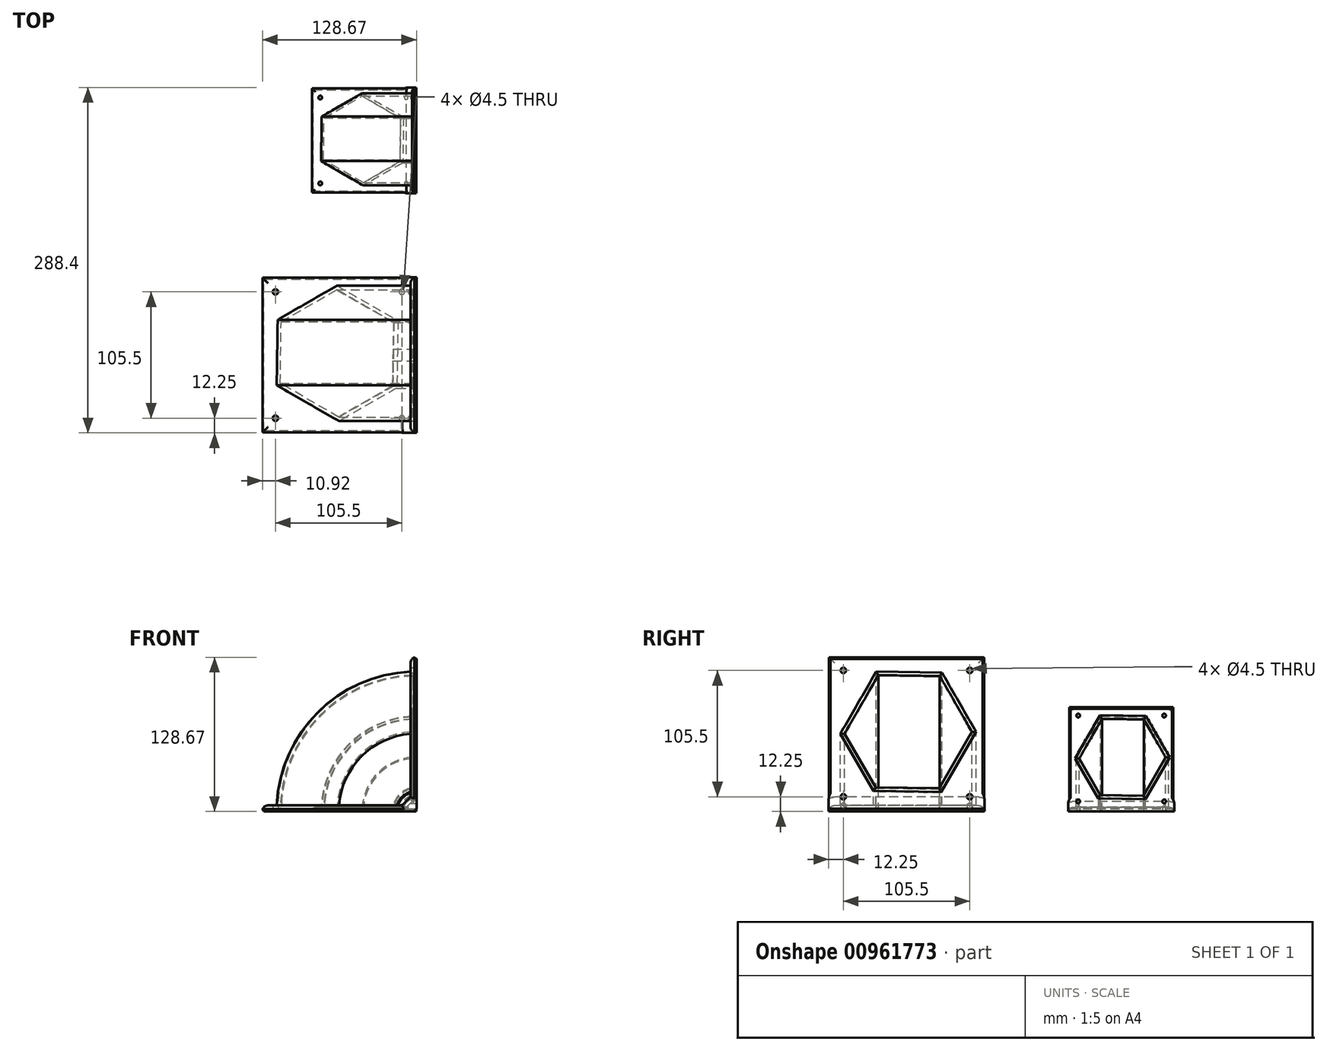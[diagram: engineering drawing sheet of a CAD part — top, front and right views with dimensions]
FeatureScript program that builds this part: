
annotation { "Feature Type Name" : "Feature", "Feature Type Description" : "" }
export const myFeature = defineFeature(function(context is Context, id is Id, definition is map)
    precondition{}
    {
        {
            var Q0;
            Q0=qCreatedBy(makeId("Top.planeOp"),FACE);
            var sketch = newSketch(context, id + "F0", { "sketchPlane" : qUnion([Q0])});
            skCircle(sketch, "E0", {"center": v(0, 0) * mm, "radius": 60 * mm, "construction": true});
            skLineSegment(sketch, "E1.bottom", {"start": v(64.01, -65) * mm, "end": v(-64.01, -65) * mm});
            skLineSegment(sketch, "E1.top", {"start": v(64.01, 65) * mm, "end": v(-64.01, 65) * mm});
            skLineSegment(sketch, "E1.left", {"start": v(64.01, -65) * mm, "end": v(64.01, 65) * mm});
            skLineSegment(sketch, "E1.right", {"start": v(-64.01, -65) * mm, "end": v(-64.01, 65) * mm});
            skCircle(sketch, "E2.0", {"center": v(0, 0) * mm, "radius": 55.2 * mm, "construction": true});
            skLineSegment(sketch, "E3.bottom", {"start": v(52.75, 52.75) * mm, "end": v(-52.75, 52.75) * mm, "construction": true});
            skLineSegment(sketch, "E3.top", {"start": v(52.75, -52.75) * mm, "end": v(-52.75, -52.75) * mm, "construction": true});
            skLineSegment(sketch, "E3.left", {"start": v(52.75, 52.75) * mm, "end": v(52.75, -52.75) * mm, "construction": true});
            skLineSegment(sketch, "E3.right", {"start": v(-52.75, 52.75) * mm, "end": v(-52.75, -52.75) * mm, "construction": true});
            skCircle(sketch, "E4", {"center": v(52.75, -52.75) * mm, "radius": 2.25 * mm});
            skCircle(sketch, "E5", {"center": v(-52.75, -52.75) * mm, "radius": 2.25 * mm});
            skCircle(sketch, "E6", {"center": v(-52.75, 52.75) * mm, "radius": 2.25 * mm});
            skCircle(sketch, "E7", {"center": v(52.75, 52.75) * mm, "radius": 2.25 * mm});
            skPoint(sketch, "E8.cCircle.perimeterSnap0", {"position": v(0, -52.75) * mm});
            skLineSegment(sketch, "E8.0", {"start": v(0, -55.2) * mm, "end": v(-51.87, -25.25) * mm});
            skPoint(sketch, "E8.0.startSnap0", {"position": v(0, -52.75) * mm});
            skLineSegment(sketch, "E8.1", {"start": v(-51.87, -25.25) * mm, "end": v(-51.03, 29.5) * mm});
            skLineSegment(sketch, "E8.2", {"start": v(-51.03, 29.5) * mm, "end": v(-1.63, 58.01) * mm});
            skLineSegment(sketch, "E8.3", {"start": v(-1.63, 58.01) * mm, "end": v(48.73, 28.94) * mm});
            skLineSegment(sketch, "E8.4", {"start": v(48.73, 28.94) * mm, "end": v(47.8, -27.6) * mm});
            skLineSegment(sketch, "E8.5", {"start": v(47.8, -27.6) * mm, "end": v(0, -55.2) * mm});
            skLineSegment(sketch, "E9.0", {"start": v(-48.84, -23.54) * mm, "end": v(-48.05, 27.74) * mm});
            skLineSegment(sketch, "E9.1", {"start": v(-1.63, 54.55) * mm, "end": v(45.7, 27.23) * mm});
            skLineSegment(sketch, "E9.2", {"start": v(45.7, 27.23) * mm, "end": v(44.83, -25.85) * mm});
            skLineSegment(sketch, "E9.3", {"start": v(-48.05, 27.74) * mm, "end": v(-1.63, 54.55) * mm});
            skLineSegment(sketch, "E9.4", {"start": v(44.83, -25.85) * mm, "end": v(0, -51.74) * mm});
            skLineSegment(sketch, "E9.5", {"start": v(0, -51.74) * mm, "end": v(-48.84, -23.54) * mm});
            skSolve(sketch);
        }
        {
            var Q0;
            Q0=qCreatedBy(makeId("Front.planeOp"),FACE);
            var sketch = newSketch(context, id + "F1", { "sketchPlane" : qUnion([Q0])});
            skLineSegment(sketch, "E10.bottom", {"start": v(0, 0) * mm, "end": v(65, 0) * mm, "construction": true});
            skLineSegment(sketch, "E10.top", {"start": v(0, 65) * mm, "end": v(65, 65) * mm, "construction": true});
            skLineSegment(sketch, "E10.left", {"start": v(0, 0) * mm, "end": v(0, 65) * mm, "construction": true});
            skLineSegment(sketch, "E10.right", {"start": v(65, 0) * mm, "end": v(65, 65) * mm, "construction": true});
            skArc(sketch, "E11", {"start": v(19.04, 45.96) * mm, "mid": v(4.95, 24.87) * mm, "end": v(0, 0) * mm});
            skLineSegment(sketch, "E12", {"start": v(0, 65) * mm, "end": v(65, 0) * mm, "construction": true});
            skSolve(sketch);
        }
        {
            var Q0;
            Q0=makeQuery(id+"F0.imprint","IMPRINT",FACE,{"disambiguationData":[TD([[makeQuery(id+"F0.imprint","IMPRINT",EDGE,{"derivedFrom":sQuery(id+"F0.wireOp",EDGE,"E8.0")}),-1.0]])]});
            var Q1;
            Q1=sQuery(id+"F1.wireOp",EDGE,"E11");
            sweep(context, id + "F2", {"profiles" : qUnion([Q0]), "path" : qUnion([Q1])});
        }
        {
            var Q0;
            Q0=makeQuery(id+"F0.imprint","IMPRINT",FACE,{"disambiguationData":[TD([[makeQuery(id+"F0.imprint","IMPRINT",EDGE,{"derivedFrom":sQuery(id+"F0.wireOp",EDGE,"E1.bottom")}),-1.0]])]});
            var Q1;
            Q1=makeQuery(id+"F0.imprint","IMPRINT",FACE,{"disambiguationData":[TD([[makeQuery(id+"F0.imprint","IMPRINT",EDGE,{"derivedFrom":sQuery(id+"F0.wireOp",EDGE,"E8.0")}),-1.0]])]});
            extrude(context, id + "F3", {"entities" : qUnion([Q0, Q1]), "operationType" : NewBodyOperationType.ADD, "depth" : 5 * mm, "offsetDistance" : 25 * mm});
        }
        {
            var Q0;
            Q0=makeQuery(id+"F2.opSweep","CAP_FACE",FACE,{"disambiguationData":[OSD([sQuery(id+"F0.wireOp",EDGE,"E0"),sQuery(id+"F0.wireOp",EDGE,"E2.0"),sQuery(id+"F1.wireOp",VERTEX,"E11.start")])],"isStart":false});
            cPlane(context, id + "F4", {"entities" : qUnion([Q0]), "cplaneType" : CPlaneType.OFFSET, "offset" : 0 * mm, "width" : 150 * mm, "height" : 150 * mm});
        }
        {
            var Q0;
            Q0=makeQuery(id+"F2.opSweep","SWEPT_BODY",BODY,{"disambiguationData":[OSD([sQuery(id+"F0.wireOp",EDGE,"E0"),sQuery(id+"F0.wireOp",EDGE,"E2.0"),sQuery(id+"F1.wireOp",EDGE,"E11")])]});
            var Q1;
            Q1=qCreatedBy(id+"F4.planeOp",FACE);
            mirror(context, id + "F5", {"operationType" : NewBodyOperationType.ADD, "entities" : qUnion([Q0]), "mirrorPlane" : qUnion([Q1])});
        }
        {
            var Q0;
            {var subQ0=sQuery(id+"F0.wireOp",EDGE,"E1.top");var subQ1=sQuery(id+"F0.wireOp",EDGE,"E1.bottom");var subQ3=sQuery(id+"F0.wireOp",EDGE,"E6");var subQ4=sQuery(id+"F0.wireOp",EDGE,"E2.0");var subQ5=sQuery(id+"F0.wireOp",EDGE,"E4");var subQ6=sQuery(id+"F0.wireOp",EDGE,"E1.left");var subQ7=sQuery(id+"F0.wireOp",EDGE,"E1.right");var subQ8=sQuery(id+"F0.wireOp",EDGE,"E5");var subQ9=sQuery(id+"F0.wireOp",EDGE,"E7");var subQ10=makeQuery(id+"F3.boolean.opBoolean","SPLIT",FACE,{"disambiguationData":[TD([makeQuery(id+"F3.opExtrude","SWEPT_FACE",FACE,{"disambiguationData":[OSD([subQ1])]})])],"derivedFrom":makeQuery(id+"F3.opExtrude","CAP_FACE",FACE,{"disambiguationData":[OSD([subQ1,subQ0,subQ6,subQ7,subQ4,subQ5,subQ8,subQ3,subQ9])],"isStart":false})});Q0=makeQuery(id+"F5.boolean.opBoolean","INTERSECT",EDGE,{"disambiguationData":[OD(0.0)],"derivedFrom":[subQ10,makeQuery(id+"F5.opPattern","COPY",FACE,{"derivedFrom":subQ10,"instanceName":"1"})]});}
            var Q1;
            {var subQ0=sQuery(id+"F0.wireOp",EDGE,"E1.top");var subQ1=sQuery(id+"F0.wireOp",EDGE,"E1.bottom");var subQ3=sQuery(id+"F0.wireOp",EDGE,"E6");var subQ4=sQuery(id+"F0.wireOp",EDGE,"E2.0");var subQ5=sQuery(id+"F0.wireOp",EDGE,"E4");var subQ6=sQuery(id+"F0.wireOp",EDGE,"E1.left");var subQ7=sQuery(id+"F0.wireOp",EDGE,"E1.right");var subQ8=sQuery(id+"F0.wireOp",EDGE,"E5");var subQ9=sQuery(id+"F0.wireOp",EDGE,"E7");var subQ10=makeQuery(id+"F3.boolean.opBoolean","SPLIT",FACE,{"disambiguationData":[TD([makeQuery(id+"F3.opExtrude","SWEPT_FACE",FACE,{"disambiguationData":[OSD([subQ1])]})])],"derivedFrom":makeQuery(id+"F3.opExtrude","CAP_FACE",FACE,{"disambiguationData":[OSD([subQ1,subQ0,subQ6,subQ7,subQ4,subQ5,subQ8,subQ3,subQ9])],"isStart":false})});Q1=makeQuery(id+"F5.boolean.opBoolean","INTERSECT",EDGE,{"disambiguationData":[OD(1.0)],"derivedFrom":[subQ10,makeQuery(id+"F5.opPattern","COPY",FACE,{"derivedFrom":subQ10,"instanceName":"1"})]});}
            chamfer(context, id + "F6", {"entities" : qUnion([Q0, Q1]), "width" : 7 * mm, "tangentPropagation" : true});
        }
        {
            var Q0;
            {var subQ0=sQuery(id+"F0.wireOp",EDGE,"E0");var subQ1=makeQuery(id+"F2.opSweep","SWEPT_FACE",FACE,{"disambiguationData":[OSD([subQ0,sQuery(id+"F1.wireOp",EDGE,"E11")])]});var subQ2=subQ1;var subQ3=sQuery(id+"F0.wireOp",EDGE,"E1.top");var subQ4=sQuery(id+"F0.wireOp",EDGE,"E1.bottom");var subQ5=sQuery(id+"F0.wireOp",EDGE,"E6");var subQ6=sQuery(id+"F0.wireOp",EDGE,"E2.0");var subQ7=sQuery(id+"F0.wireOp",EDGE,"E4");var subQ8=sQuery(id+"F0.wireOp",EDGE,"E1.left");var subQ9=sQuery(id+"F0.wireOp",EDGE,"E1.right");var subQ10=sQuery(id+"F0.wireOp",EDGE,"E5");var subQ11=sQuery(id+"F0.wireOp",EDGE,"E7");var subQ12=makeQuery(id+"F3.boolean.opBoolean","SPLIT",FACE,{"disambiguationData":[TD([makeQuery(id+"F3.opExtrude","SWEPT_FACE",FACE,{"disambiguationData":[OSD([subQ4])]})])],"derivedFrom":makeQuery(id+"F3.opExtrude","CAP_FACE",FACE,{"disambiguationData":[OSD([subQ4,subQ3,subQ8,subQ9,subQ6,subQ7,subQ10,subQ5,subQ11])],"isStart":false})});Q0=makeQuery(id+"F6.opChamfer","BLEND_EDGE",EDGE,{"blendedFrom":[makeQuery(id+"F5.boolean.opBoolean","INTERSECT",EDGE,{"disambiguationData":[OD(1.0)],"derivedFrom":[subQ12,makeQuery(id+"F5.opPattern","COPY",FACE,{"derivedFrom":subQ12,"instanceName":"1"})]}),makeQuery(id+"F5.boolean.opBoolean","MERGE",FACE,{"derivedFrom":[subQ2,makeQuery(id+"F5.opPattern","COPY",FACE,{"derivedFrom":subQ2,"instanceName":"1"})]})],"blendedInto":[makeQuery(id+"F5.boolean.opBoolean","MERGE",FACE,{"derivedFrom":[subQ2,makeQuery(id+"F5.opPattern","COPY",FACE,{"derivedFrom":subQ2,"instanceName":"1"})]})]});}
            var Q1;
            {var subQ0=sQuery(id+"F0.wireOp",EDGE,"E0");var subQ1=makeQuery(id+"F2.opSweep","SWEPT_FACE",FACE,{"disambiguationData":[OSD([subQ0,sQuery(id+"F1.wireOp",EDGE,"E11")])]});var subQ2=subQ1;var subQ3=sQuery(id+"F0.wireOp",EDGE,"E1.top");var subQ4=sQuery(id+"F0.wireOp",EDGE,"E1.bottom");var subQ5=sQuery(id+"F0.wireOp",EDGE,"E6");var subQ6=sQuery(id+"F0.wireOp",EDGE,"E2.0");var subQ7=sQuery(id+"F0.wireOp",EDGE,"E4");var subQ8=sQuery(id+"F0.wireOp",EDGE,"E1.left");var subQ9=sQuery(id+"F0.wireOp",EDGE,"E1.right");var subQ10=sQuery(id+"F0.wireOp",EDGE,"E5");var subQ11=sQuery(id+"F0.wireOp",EDGE,"E7");var subQ12=makeQuery(id+"F3.boolean.opBoolean","SPLIT",FACE,{"disambiguationData":[TD([makeQuery(id+"F3.opExtrude","SWEPT_FACE",FACE,{"disambiguationData":[OSD([subQ4])]})])],"derivedFrom":makeQuery(id+"F3.opExtrude","CAP_FACE",FACE,{"disambiguationData":[OSD([subQ4,subQ3,subQ8,subQ9,subQ6,subQ7,subQ10,subQ5,subQ11])],"isStart":false})});Q1=makeQuery(id+"F6.opChamfer","BLEND_EDGE",EDGE,{"blendedFrom":[makeQuery(id+"F5.boolean.opBoolean","INTERSECT",EDGE,{"disambiguationData":[OD(0.0)],"derivedFrom":[subQ12,makeQuery(id+"F5.opPattern","COPY",FACE,{"derivedFrom":subQ12,"instanceName":"1"})]}),makeQuery(id+"F5.boolean.opBoolean","MERGE",FACE,{"derivedFrom":[subQ2,makeQuery(id+"F5.opPattern","COPY",FACE,{"derivedFrom":subQ2,"instanceName":"1"})]})],"blendedInto":[makeQuery(id+"F5.boolean.opBoolean","MERGE",FACE,{"derivedFrom":[subQ2,makeQuery(id+"F5.opPattern","COPY",FACE,{"derivedFrom":subQ2,"instanceName":"1"})]})]});}
            var Q2;
            Q2=makeQuery(id+"F3.opExtrude","CAP_EDGE",EDGE,{"disambiguationData":[OSD([sQuery(id+"F0.wireOp",EDGE,"E1.bottom")])],"isStart":false});
            var Q3;
            Q3=makeQuery(id+"F5.opPattern","COPY",EDGE,{"derivedFrom":makeQuery(id+"F3.opExtrude","CAP_EDGE",EDGE,{"disambiguationData":[OSD([sQuery(id+"F0.wireOp",EDGE,"E1.bottom")])],"isStart":false}),"instanceName":"1"});
            var Q4;
            Q4=makeQuery(id+"F5.opPattern","COPY",EDGE,{"derivedFrom":makeQuery(id+"F3.opExtrude","CAP_EDGE",EDGE,{"disambiguationData":[OSD([sQuery(id+"F0.wireOp",EDGE,"E1.top")])],"isStart":false}),"instanceName":"1"});
            var Q5;
            Q5=makeQuery(id+"F5.opPattern","COPY",EDGE,{"derivedFrom":makeQuery(id+"F3.opExtrude","CAP_EDGE",EDGE,{"disambiguationData":[OSD([sQuery(id+"F0.wireOp",EDGE,"E1.right")])],"isStart":false}),"instanceName":"1"});
            var Q6;
            Q6=makeQuery(id+"F3.opExtrude","CAP_EDGE",EDGE,{"disambiguationData":[OSD([sQuery(id+"F0.wireOp",EDGE,"E1.top")])],"isStart":false});
            var Q7;
            {var subQ0=sQuery(id+"F0.wireOp",EDGE,"E1.top");var subQ1=makeQuery(id+"F3.opExtrude","SWEPT_FACE",FACE,{"disambiguationData":[OSD([subQ0])]});var subQ2=sQuery(id+"F0.wireOp",EDGE,"E1.bottom");var subQ4=sQuery(id+"F0.wireOp",EDGE,"E6");var subQ5=sQuery(id+"F0.wireOp",EDGE,"E2.0");var subQ6=sQuery(id+"F0.wireOp",EDGE,"E4");var subQ7=sQuery(id+"F0.wireOp",EDGE,"E1.left");var subQ8=sQuery(id+"F0.wireOp",EDGE,"E1.right");var subQ9=sQuery(id+"F0.wireOp",EDGE,"E5");var subQ10=sQuery(id+"F0.wireOp",EDGE,"E7");var subQ11=makeQuery(id+"F3.boolean.opBoolean","SPLIT",FACE,{"disambiguationData":[TD([makeQuery(id+"F3.opExtrude","SWEPT_FACE",FACE,{"disambiguationData":[OSD([subQ2])]})])],"derivedFrom":makeQuery(id+"F3.opExtrude","CAP_FACE",FACE,{"disambiguationData":[OSD([subQ2,subQ0,subQ7,subQ8,subQ5,subQ6,subQ9,subQ4,subQ10])],"isStart":false})});Q7=makeQuery(id+"F6.opChamfer","BLEND_EDGE",EDGE,{"blendedFrom":[makeQuery(id+"F5.boolean.opBoolean","INTERSECT",EDGE,{"disambiguationData":[OD(1.0)],"derivedFrom":[subQ11,makeQuery(id+"F5.opPattern","COPY",FACE,{"derivedFrom":subQ11,"instanceName":"1"})]}),makeQuery(id+"F5.boolean.opBoolean","MERGE",FACE,{"derivedFrom":[subQ1,makeQuery(id+"F5.opPattern","COPY",FACE,{"derivedFrom":subQ1,"instanceName":"1"})]})],"blendedInto":[makeQuery(id+"F5.boolean.opBoolean","MERGE",FACE,{"derivedFrom":[subQ1,makeQuery(id+"F5.opPattern","COPY",FACE,{"derivedFrom":subQ1,"instanceName":"1"})]})]});}
            var Q8;
            {var subQ0=sQuery(id+"F0.wireOp",EDGE,"E1.bottom");var subQ1=makeQuery(id+"F3.opExtrude","SWEPT_FACE",FACE,{"disambiguationData":[OSD([subQ0])]});var subQ2=sQuery(id+"F0.wireOp",EDGE,"E1.top");var subQ4=sQuery(id+"F0.wireOp",EDGE,"E6");var subQ5=sQuery(id+"F0.wireOp",EDGE,"E2.0");var subQ6=sQuery(id+"F0.wireOp",EDGE,"E4");var subQ7=sQuery(id+"F0.wireOp",EDGE,"E1.left");var subQ8=sQuery(id+"F0.wireOp",EDGE,"E1.right");var subQ9=sQuery(id+"F0.wireOp",EDGE,"E5");var subQ10=sQuery(id+"F0.wireOp",EDGE,"E7");var subQ11=makeQuery(id+"F3.boolean.opBoolean","SPLIT",FACE,{"disambiguationData":[TD([subQ1])],"derivedFrom":makeQuery(id+"F3.opExtrude","CAP_FACE",FACE,{"disambiguationData":[OSD([subQ0,subQ2,subQ7,subQ8,subQ5,subQ6,subQ9,subQ4,subQ10])],"isStart":false})});Q8=makeQuery(id+"F6.opChamfer","BLEND_EDGE",EDGE,{"blendedFrom":[makeQuery(id+"F5.boolean.opBoolean","INTERSECT",EDGE,{"disambiguationData":[OD(0.0)],"derivedFrom":[subQ11,makeQuery(id+"F5.opPattern","COPY",FACE,{"derivedFrom":subQ11,"instanceName":"1"})]}),makeQuery(id+"F5.boolean.opBoolean","MERGE",FACE,{"derivedFrom":[subQ1,makeQuery(id+"F5.opPattern","COPY",FACE,{"derivedFrom":subQ1,"instanceName":"1"})]})],"blendedInto":[makeQuery(id+"F5.boolean.opBoolean","MERGE",FACE,{"derivedFrom":[subQ1,makeQuery(id+"F5.opPattern","COPY",FACE,{"derivedFrom":subQ1,"instanceName":"1"})]})]});}
            var Q9;
            Q9=makeQuery(id+"F3.opExtrude","CAP_EDGE",EDGE,{"disambiguationData":[OSD([sQuery(id+"F0.wireOp",EDGE,"E1.right")])],"isStart":false});
            fillet(context, id + "F7", {"entities" : qUnion([Q0, Q1, Q2, Q3, Q4, Q5, Q6, Q7, Q8, Q9]), "radius" : 5 * mm, "tangentPropagation" : true, "allowEdgeOverflow" : false});
        }
        {
            var Q0;
            Q0=makeQuery(id+"F2.opSweep","SWEPT_BODY",BODY,{"disambiguationData":[OSD([sQuery(id+"F0.wireOp",EDGE,"E0"),sQuery(id+"F0.wireOp",EDGE,"E2.0"),sQuery(id+"F1.wireOp",EDGE,"E11")])]});
            transform(context, id + "F8", {"entities" : qUnion([Q0]), "transformType" : TransformType.TRANSLATION_3D, "dx" : 0 * mm, "dy" : 200 * mm, "dz" : 0 * mm, "makeCopy" : true});
        }
        {
            var Q0;
            Q0=makeQuery(id+"F8.opPattern","COPY",BODY,{"derivedFrom":makeQuery(id+"F2.opSweep","SWEPT_BODY",BODY,{"disambiguationData":[OSD([sQuery(id+"F0.wireOp",EDGE,"E0"),sQuery(id+"F0.wireOp",EDGE,"E2.0"),sQuery(id+"F1.wireOp",EDGE,"E11")])]}),"instanceName":"1"});
            var Q1;
            Q1=makeQuery(id+"F8.opPattern","COPY",VERTEX,{"derivedFrom":makeQuery(id+"F3.opExtrude","CAP_VERTEX",VERTEX,{"disambiguationData":[OSD([sQuery(id+"F0.wireOp",EDGE,"E1.bottom"),sQuery(id+"F0.wireOp",EDGE,"E1.left")])],"isStart":true}),"instanceName":"1"});
            transform(context, id + "F9", {"entities" : qUnion([Q0]), "transformType" : TransformType.SCALE_UNIFORMLY, "scale" : 0.68, "scalePoint" : qUnion([Q1]), "makeCopy" : false});
        }
        {
            var Q0;
            {var subQ0=sQuery(id+"F0.wireOp",EDGE,"E2.0");Q0=makeQuery(id+"F5.opPattern","COPY",FACE,{"derivedFrom":makeQuery(id+"F3.boolean.opBoolean","MERGE",FACE,{"derivedFrom":[makeQuery(id+"F2.opSweep","CAP_FACE",FACE,{"disambiguationData":[OSD([sQuery(id+"F0.wireOp",EDGE,"E0"),subQ0,sQuery(id+"F1.wireOp",VERTEX,"E11.end")])],"isStart":true}),makeQuery(id+"F3.opExtrude","CAP_FACE",FACE,{"disambiguationData":[OSD([sQuery(id+"F0.wireOp",EDGE,"E1.bottom"),sQuery(id+"F0.wireOp",EDGE,"E1.top"),sQuery(id+"F0.wireOp",EDGE,"E1.left"),sQuery(id+"F0.wireOp",EDGE,"E1.right"),subQ0,sQuery(id+"F0.wireOp",EDGE,"E4"),sQuery(id+"F0.wireOp",EDGE,"E5"),sQuery(id+"F0.wireOp",EDGE,"E6"),sQuery(id+"F0.wireOp",EDGE,"E7")])],"isStart":true})]}),"instanceName":"1"});}
            var sketch = newSketch(context, id + "F10", { "sketchPlane" : qUnion([Q0])});
            skArc(sketch, "E13", {"start": v(5, 0.99) * mm, "mid": v(0, 2.33) * mm, "end": v(-5, 0.99) * mm});
            skLineSegment(sketch, "E14", {"start": v(-5, 0.99) * mm, "end": v(-5, 0) * mm});
            skLineSegment(sketch, "E15", {"start": v(-5, 0) * mm, "end": v(5, 0) * mm});
            skLineSegment(sketch, "E16", {"start": v(5, 0) * mm, "end": v(5, 0.99) * mm});
            skSolve(sketch);
        }
        {
            var Q0;
            {var subQ0=sQuery(id+"F10.wireOp",EDGE,"E13");Q0=makeQuery(id+"F10.imprint","IMPRINT",FACE,{"disambiguationData":[TD([[makeQuery(id+"F10.imprint","IMPRINT",EDGE,{"derivedFrom":subQ0}),1.0]])]});}
            var Q1;
            {var subQ0=sQuery(id+"F10.wireOp",EDGE,"E14");Q1=makeQuery(id+"F10.imprint","IMPRINT",FACE,{"disambiguationData":[TD([[makeQuery(id+"F10.imprint","IMPRINT",EDGE,{"derivedFrom":subQ0}),1.0]])]});}
            extrude(context, id + "F11", {"entities" : qUnion([Q0, Q1]), "operationType" : NewBodyOperationType.REMOVE, "oppositeDirection" : true, "depth" : 25 * mm, "offsetDistance" : 25 * mm});
        }
        {
            var Q0;
            {var subQ1=sQuery(id+"F0.wireOp",EDGE,"E1.left");var subQ2=sQuery(id+"F0.wireOp",EDGE,"E1.top");var subQ3=makeQuery(id+"F3.opExtrude","SWEPT_FACE",FACE,{"disambiguationData":[OSD([subQ2])]});Q0=makeQuery(id+"F11.boolean.opBoolean","SPLIT",EDGE,{"disambiguationData":[TD([subQ3])],"derivedFrom":makeQuery(id+"F5.opPattern","COPY",EDGE,{"derivedFrom":makeQuery(id+"F3.opExtrude","CAP_EDGE",EDGE,{"disambiguationData":[OSD([subQ1])],"isStart":true}),"instanceName":"1"})});}
            var Q1;
            {var subQ1=sQuery(id+"F0.wireOp",EDGE,"E1.left");var subQ2=sQuery(id+"F0.wireOp",EDGE,"E1.bottom");var subQ3=makeQuery(id+"F3.opExtrude","SWEPT_FACE",FACE,{"disambiguationData":[OSD([subQ2])]});Q1=makeQuery(id+"F11.boolean.opBoolean","SPLIT",EDGE,{"disambiguationData":[TD([subQ3])],"derivedFrom":makeQuery(id+"F5.opPattern","COPY",EDGE,{"derivedFrom":makeQuery(id+"F3.opExtrude","CAP_EDGE",EDGE,{"disambiguationData":[OSD([subQ1])],"isStart":true}),"instanceName":"1"})});}
            var Q2;
            {var subQ0=sQuery(id+"F0.wireOp",EDGE,"E9.5");var subQ1=sQuery(id+"F0.wireOp",EDGE,"E9.4");var subQ2=sQuery(id+"F0.wireOp",EDGE,"E9.3");var subQ3=sQuery(id+"F0.wireOp",EDGE,"E9.2");var subQ4=sQuery(id+"F0.wireOp",EDGE,"E9.1");var subQ5=sQuery(id+"F0.wireOp",EDGE,"E9.0");var subQ6=sQuery(id+"F0.wireOp",EDGE,"E1.top");Q2=makeQuery(id+"F7.opFillet","BLEND_EDGE",EDGE,{"blendedFrom":[makeQuery(id+"F3.opExtrude","CAP_EDGE",EDGE,{"disambiguationData":[OSD([subQ6])],"isStart":false}),makeQuery(id+"F3.boolean.opBoolean","MERGE",FACE,{"derivedFrom":[makeQuery(id+"F2.opSweep","CAP_FACE",FACE,{"disambiguationData":[OSD([sQuery(id+"F0.wireOp",EDGE,"E8.0"),sQuery(id+"F0.wireOp",EDGE,"E8.1"),sQuery(id+"F0.wireOp",EDGE,"E8.2"),sQuery(id+"F0.wireOp",EDGE,"E8.3"),sQuery(id+"F0.wireOp",EDGE,"E8.4"),sQuery(id+"F0.wireOp",EDGE,"E8.5"),subQ5,subQ4,subQ3,subQ2,subQ1,subQ0,sQuery(id+"F1.wireOp",VERTEX,"E11.end")])],"isStart":true}),makeQuery(id+"F3.opExtrude","CAP_FACE",FACE,{"disambiguationData":[OSD([sQuery(id+"F0.wireOp",EDGE,"E1.bottom"),subQ6,sQuery(id+"F0.wireOp",EDGE,"E1.left"),sQuery(id+"F0.wireOp",EDGE,"E1.right"),sQuery(id+"F0.wireOp",EDGE,"E4"),sQuery(id+"F0.wireOp",EDGE,"E5"),sQuery(id+"F0.wireOp",EDGE,"E6"),sQuery(id+"F0.wireOp",EDGE,"E7"),subQ5,subQ4,subQ3,subQ2,subQ1,subQ0])],"isStart":true})]})],"blendedInto":[makeQuery(id+"F3.boolean.opBoolean","MERGE",FACE,{"derivedFrom":[makeQuery(id+"F2.opSweep","CAP_FACE",FACE,{"disambiguationData":[OSD([sQuery(id+"F0.wireOp",EDGE,"E8.0"),sQuery(id+"F0.wireOp",EDGE,"E8.1"),sQuery(id+"F0.wireOp",EDGE,"E8.2"),sQuery(id+"F0.wireOp",EDGE,"E8.3"),sQuery(id+"F0.wireOp",EDGE,"E8.4"),sQuery(id+"F0.wireOp",EDGE,"E8.5"),subQ5,subQ4,subQ3,subQ2,subQ1,subQ0,sQuery(id+"F1.wireOp",VERTEX,"E11.end")])],"isStart":true}),makeQuery(id+"F3.opExtrude","CAP_FACE",FACE,{"disambiguationData":[OSD([sQuery(id+"F0.wireOp",EDGE,"E1.bottom"),subQ6,sQuery(id+"F0.wireOp",EDGE,"E1.left"),sQuery(id+"F0.wireOp",EDGE,"E1.right"),sQuery(id+"F0.wireOp",EDGE,"E4"),sQuery(id+"F0.wireOp",EDGE,"E5"),sQuery(id+"F0.wireOp",EDGE,"E6"),sQuery(id+"F0.wireOp",EDGE,"E7"),subQ5,subQ4,subQ3,subQ2,subQ1,subQ0])],"isStart":true})]})]});}
            var Q3;
            {var subQ0=sQuery(id+"F0.wireOp",EDGE,"E9.5");var subQ1=sQuery(id+"F0.wireOp",EDGE,"E9.4");var subQ2=sQuery(id+"F0.wireOp",EDGE,"E9.3");var subQ3=sQuery(id+"F0.wireOp",EDGE,"E9.2");var subQ4=sQuery(id+"F0.wireOp",EDGE,"E9.1");var subQ5=sQuery(id+"F0.wireOp",EDGE,"E9.0");var subQ6=sQuery(id+"F0.wireOp",EDGE,"E1.right");Q3=makeQuery(id+"F7.opFillet","BLEND_EDGE",EDGE,{"blendedFrom":[makeQuery(id+"F3.opExtrude","CAP_EDGE",EDGE,{"disambiguationData":[OSD([subQ6])],"isStart":false}),makeQuery(id+"F3.boolean.opBoolean","MERGE",FACE,{"derivedFrom":[makeQuery(id+"F2.opSweep","CAP_FACE",FACE,{"disambiguationData":[OSD([sQuery(id+"F0.wireOp",EDGE,"E8.0"),sQuery(id+"F0.wireOp",EDGE,"E8.1"),sQuery(id+"F0.wireOp",EDGE,"E8.2"),sQuery(id+"F0.wireOp",EDGE,"E8.3"),sQuery(id+"F0.wireOp",EDGE,"E8.4"),sQuery(id+"F0.wireOp",EDGE,"E8.5"),subQ5,subQ4,subQ3,subQ2,subQ1,subQ0,sQuery(id+"F1.wireOp",VERTEX,"E11.end")])],"isStart":true}),makeQuery(id+"F3.opExtrude","CAP_FACE",FACE,{"disambiguationData":[OSD([sQuery(id+"F0.wireOp",EDGE,"E1.bottom"),sQuery(id+"F0.wireOp",EDGE,"E1.top"),sQuery(id+"F0.wireOp",EDGE,"E1.left"),subQ6,sQuery(id+"F0.wireOp",EDGE,"E4"),sQuery(id+"F0.wireOp",EDGE,"E5"),sQuery(id+"F0.wireOp",EDGE,"E6"),sQuery(id+"F0.wireOp",EDGE,"E7"),subQ5,subQ4,subQ3,subQ2,subQ1,subQ0])],"isStart":true})]})],"blendedInto":[makeQuery(id+"F3.boolean.opBoolean","MERGE",FACE,{"derivedFrom":[makeQuery(id+"F2.opSweep","CAP_FACE",FACE,{"disambiguationData":[OSD([sQuery(id+"F0.wireOp",EDGE,"E8.0"),sQuery(id+"F0.wireOp",EDGE,"E8.1"),sQuery(id+"F0.wireOp",EDGE,"E8.2"),sQuery(id+"F0.wireOp",EDGE,"E8.3"),sQuery(id+"F0.wireOp",EDGE,"E8.4"),sQuery(id+"F0.wireOp",EDGE,"E8.5"),subQ5,subQ4,subQ3,subQ2,subQ1,subQ0,sQuery(id+"F1.wireOp",VERTEX,"E11.end")])],"isStart":true}),makeQuery(id+"F3.opExtrude","CAP_FACE",FACE,{"disambiguationData":[OSD([sQuery(id+"F0.wireOp",EDGE,"E1.bottom"),sQuery(id+"F0.wireOp",EDGE,"E1.top"),sQuery(id+"F0.wireOp",EDGE,"E1.left"),subQ6,sQuery(id+"F0.wireOp",EDGE,"E4"),sQuery(id+"F0.wireOp",EDGE,"E5"),sQuery(id+"F0.wireOp",EDGE,"E6"),sQuery(id+"F0.wireOp",EDGE,"E7"),subQ5,subQ4,subQ3,subQ2,subQ1,subQ0])],"isStart":true})]})]});}
            var Q4;
            {var subQ0=sQuery(id+"F0.wireOp",EDGE,"E9.5");var subQ1=sQuery(id+"F0.wireOp",EDGE,"E9.4");var subQ2=sQuery(id+"F0.wireOp",EDGE,"E9.3");var subQ3=sQuery(id+"F0.wireOp",EDGE,"E9.2");var subQ4=sQuery(id+"F0.wireOp",EDGE,"E9.1");var subQ5=sQuery(id+"F0.wireOp",EDGE,"E9.0");var subQ6=sQuery(id+"F0.wireOp",EDGE,"E1.bottom");Q4=makeQuery(id+"F7.opFillet","BLEND_EDGE",EDGE,{"blendedFrom":[makeQuery(id+"F3.opExtrude","CAP_EDGE",EDGE,{"disambiguationData":[OSD([subQ6])],"isStart":false}),makeQuery(id+"F3.boolean.opBoolean","MERGE",FACE,{"derivedFrom":[makeQuery(id+"F2.opSweep","CAP_FACE",FACE,{"disambiguationData":[OSD([sQuery(id+"F0.wireOp",EDGE,"E8.0"),sQuery(id+"F0.wireOp",EDGE,"E8.1"),sQuery(id+"F0.wireOp",EDGE,"E8.2"),sQuery(id+"F0.wireOp",EDGE,"E8.3"),sQuery(id+"F0.wireOp",EDGE,"E8.4"),sQuery(id+"F0.wireOp",EDGE,"E8.5"),subQ5,subQ4,subQ3,subQ2,subQ1,subQ0,sQuery(id+"F1.wireOp",VERTEX,"E11.end")])],"isStart":true}),makeQuery(id+"F3.opExtrude","CAP_FACE",FACE,{"disambiguationData":[OSD([subQ6,sQuery(id+"F0.wireOp",EDGE,"E1.top"),sQuery(id+"F0.wireOp",EDGE,"E1.left"),sQuery(id+"F0.wireOp",EDGE,"E1.right"),sQuery(id+"F0.wireOp",EDGE,"E4"),sQuery(id+"F0.wireOp",EDGE,"E5"),sQuery(id+"F0.wireOp",EDGE,"E6"),sQuery(id+"F0.wireOp",EDGE,"E7"),subQ5,subQ4,subQ3,subQ2,subQ1,subQ0])],"isStart":true})]})],"blendedInto":[makeQuery(id+"F3.boolean.opBoolean","MERGE",FACE,{"derivedFrom":[makeQuery(id+"F2.opSweep","CAP_FACE",FACE,{"disambiguationData":[OSD([sQuery(id+"F0.wireOp",EDGE,"E8.0"),sQuery(id+"F0.wireOp",EDGE,"E8.1"),sQuery(id+"F0.wireOp",EDGE,"E8.2"),sQuery(id+"F0.wireOp",EDGE,"E8.3"),sQuery(id+"F0.wireOp",EDGE,"E8.4"),sQuery(id+"F0.wireOp",EDGE,"E8.5"),subQ5,subQ4,subQ3,subQ2,subQ1,subQ0,sQuery(id+"F1.wireOp",VERTEX,"E11.end")])],"isStart":true}),makeQuery(id+"F3.opExtrude","CAP_FACE",FACE,{"disambiguationData":[OSD([subQ6,sQuery(id+"F0.wireOp",EDGE,"E1.top"),sQuery(id+"F0.wireOp",EDGE,"E1.left"),sQuery(id+"F0.wireOp",EDGE,"E1.right"),sQuery(id+"F0.wireOp",EDGE,"E4"),sQuery(id+"F0.wireOp",EDGE,"E5"),sQuery(id+"F0.wireOp",EDGE,"E6"),sQuery(id+"F0.wireOp",EDGE,"E7"),subQ5,subQ4,subQ3,subQ2,subQ1,subQ0])],"isStart":true})]})]});}
            var Q5;
            {var subQ0=sQuery(id+"F0.wireOp",EDGE,"E9.5");var subQ1=sQuery(id+"F0.wireOp",EDGE,"E9.4");var subQ2=sQuery(id+"F0.wireOp",EDGE,"E9.3");var subQ3=sQuery(id+"F0.wireOp",EDGE,"E9.2");var subQ4=sQuery(id+"F0.wireOp",EDGE,"E9.1");var subQ5=sQuery(id+"F0.wireOp",EDGE,"E9.0");var subQ6=sQuery(id+"F0.wireOp",EDGE,"E1.bottom");Q5=makeQuery(id+"F8.opPattern","COPY",EDGE,{"derivedFrom":makeQuery(id+"F7.opFillet","BLEND_EDGE",EDGE,{"blendedFrom":[makeQuery(id+"F3.opExtrude","CAP_EDGE",EDGE,{"disambiguationData":[OSD([subQ6])],"isStart":false}),makeQuery(id+"F3.boolean.opBoolean","MERGE",FACE,{"derivedFrom":[makeQuery(id+"F2.opSweep","CAP_FACE",FACE,{"disambiguationData":[OSD([sQuery(id+"F0.wireOp",EDGE,"E8.0"),sQuery(id+"F0.wireOp",EDGE,"E8.1"),sQuery(id+"F0.wireOp",EDGE,"E8.2"),sQuery(id+"F0.wireOp",EDGE,"E8.3"),sQuery(id+"F0.wireOp",EDGE,"E8.4"),sQuery(id+"F0.wireOp",EDGE,"E8.5"),subQ5,subQ4,subQ3,subQ2,subQ1,subQ0,sQuery(id+"F1.wireOp",VERTEX,"E11.end")])],"isStart":true}),makeQuery(id+"F3.opExtrude","CAP_FACE",FACE,{"disambiguationData":[OSD([subQ6,sQuery(id+"F0.wireOp",EDGE,"E1.top"),sQuery(id+"F0.wireOp",EDGE,"E1.left"),sQuery(id+"F0.wireOp",EDGE,"E1.right"),sQuery(id+"F0.wireOp",EDGE,"E4"),sQuery(id+"F0.wireOp",EDGE,"E5"),sQuery(id+"F0.wireOp",EDGE,"E6"),sQuery(id+"F0.wireOp",EDGE,"E7"),subQ5,subQ4,subQ3,subQ2,subQ1,subQ0])],"isStart":true})]})],"blendedInto":[makeQuery(id+"F3.boolean.opBoolean","MERGE",FACE,{"derivedFrom":[makeQuery(id+"F2.opSweep","CAP_FACE",FACE,{"disambiguationData":[OSD([sQuery(id+"F0.wireOp",EDGE,"E8.0"),sQuery(id+"F0.wireOp",EDGE,"E8.1"),sQuery(id+"F0.wireOp",EDGE,"E8.2"),sQuery(id+"F0.wireOp",EDGE,"E8.3"),sQuery(id+"F0.wireOp",EDGE,"E8.4"),sQuery(id+"F0.wireOp",EDGE,"E8.5"),subQ5,subQ4,subQ3,subQ2,subQ1,subQ0,sQuery(id+"F1.wireOp",VERTEX,"E11.end")])],"isStart":true}),makeQuery(id+"F3.opExtrude","CAP_FACE",FACE,{"disambiguationData":[OSD([subQ6,sQuery(id+"F0.wireOp",EDGE,"E1.top"),sQuery(id+"F0.wireOp",EDGE,"E1.left"),sQuery(id+"F0.wireOp",EDGE,"E1.right"),sQuery(id+"F0.wireOp",EDGE,"E4"),sQuery(id+"F0.wireOp",EDGE,"E5"),sQuery(id+"F0.wireOp",EDGE,"E6"),sQuery(id+"F0.wireOp",EDGE,"E7"),subQ5,subQ4,subQ3,subQ2,subQ1,subQ0])],"isStart":true})]})]}),"instanceName":"1"});}
            var Q6;
            {var subQ0=sQuery(id+"F0.wireOp",EDGE,"E9.5");var subQ1=sQuery(id+"F0.wireOp",EDGE,"E9.4");var subQ2=sQuery(id+"F0.wireOp",EDGE,"E9.3");var subQ3=sQuery(id+"F0.wireOp",EDGE,"E9.2");var subQ4=sQuery(id+"F0.wireOp",EDGE,"E9.1");var subQ5=sQuery(id+"F0.wireOp",EDGE,"E9.0");var subQ6=sQuery(id+"F0.wireOp",EDGE,"E1.right");Q6=makeQuery(id+"F8.opPattern","COPY",EDGE,{"derivedFrom":makeQuery(id+"F7.opFillet","BLEND_EDGE",EDGE,{"blendedFrom":[makeQuery(id+"F3.opExtrude","CAP_EDGE",EDGE,{"disambiguationData":[OSD([subQ6])],"isStart":false}),makeQuery(id+"F3.boolean.opBoolean","MERGE",FACE,{"derivedFrom":[makeQuery(id+"F2.opSweep","CAP_FACE",FACE,{"disambiguationData":[OSD([sQuery(id+"F0.wireOp",EDGE,"E8.0"),sQuery(id+"F0.wireOp",EDGE,"E8.1"),sQuery(id+"F0.wireOp",EDGE,"E8.2"),sQuery(id+"F0.wireOp",EDGE,"E8.3"),sQuery(id+"F0.wireOp",EDGE,"E8.4"),sQuery(id+"F0.wireOp",EDGE,"E8.5"),subQ5,subQ4,subQ3,subQ2,subQ1,subQ0,sQuery(id+"F1.wireOp",VERTEX,"E11.end")])],"isStart":true}),makeQuery(id+"F3.opExtrude","CAP_FACE",FACE,{"disambiguationData":[OSD([sQuery(id+"F0.wireOp",EDGE,"E1.bottom"),sQuery(id+"F0.wireOp",EDGE,"E1.top"),sQuery(id+"F0.wireOp",EDGE,"E1.left"),subQ6,sQuery(id+"F0.wireOp",EDGE,"E4"),sQuery(id+"F0.wireOp",EDGE,"E5"),sQuery(id+"F0.wireOp",EDGE,"E6"),sQuery(id+"F0.wireOp",EDGE,"E7"),subQ5,subQ4,subQ3,subQ2,subQ1,subQ0])],"isStart":true})]})],"blendedInto":[makeQuery(id+"F3.boolean.opBoolean","MERGE",FACE,{"derivedFrom":[makeQuery(id+"F2.opSweep","CAP_FACE",FACE,{"disambiguationData":[OSD([sQuery(id+"F0.wireOp",EDGE,"E8.0"),sQuery(id+"F0.wireOp",EDGE,"E8.1"),sQuery(id+"F0.wireOp",EDGE,"E8.2"),sQuery(id+"F0.wireOp",EDGE,"E8.3"),sQuery(id+"F0.wireOp",EDGE,"E8.4"),sQuery(id+"F0.wireOp",EDGE,"E8.5"),subQ5,subQ4,subQ3,subQ2,subQ1,subQ0,sQuery(id+"F1.wireOp",VERTEX,"E11.end")])],"isStart":true}),makeQuery(id+"F3.opExtrude","CAP_FACE",FACE,{"disambiguationData":[OSD([sQuery(id+"F0.wireOp",EDGE,"E1.bottom"),sQuery(id+"F0.wireOp",EDGE,"E1.top"),sQuery(id+"F0.wireOp",EDGE,"E1.left"),subQ6,sQuery(id+"F0.wireOp",EDGE,"E4"),sQuery(id+"F0.wireOp",EDGE,"E5"),sQuery(id+"F0.wireOp",EDGE,"E6"),sQuery(id+"F0.wireOp",EDGE,"E7"),subQ5,subQ4,subQ3,subQ2,subQ1,subQ0])],"isStart":true})]})]}),"instanceName":"1"});}
            var Q7;
            {var subQ0=sQuery(id+"F0.wireOp",EDGE,"E9.5");var subQ1=sQuery(id+"F0.wireOp",EDGE,"E9.4");var subQ2=sQuery(id+"F0.wireOp",EDGE,"E9.3");var subQ3=sQuery(id+"F0.wireOp",EDGE,"E9.2");var subQ4=sQuery(id+"F0.wireOp",EDGE,"E9.1");var subQ5=sQuery(id+"F0.wireOp",EDGE,"E9.0");var subQ6=sQuery(id+"F0.wireOp",EDGE,"E1.top");Q7=makeQuery(id+"F8.opPattern","COPY",EDGE,{"derivedFrom":makeQuery(id+"F7.opFillet","BLEND_EDGE",EDGE,{"blendedFrom":[makeQuery(id+"F3.opExtrude","CAP_EDGE",EDGE,{"disambiguationData":[OSD([subQ6])],"isStart":false}),makeQuery(id+"F3.boolean.opBoolean","MERGE",FACE,{"derivedFrom":[makeQuery(id+"F2.opSweep","CAP_FACE",FACE,{"disambiguationData":[OSD([sQuery(id+"F0.wireOp",EDGE,"E8.0"),sQuery(id+"F0.wireOp",EDGE,"E8.1"),sQuery(id+"F0.wireOp",EDGE,"E8.2"),sQuery(id+"F0.wireOp",EDGE,"E8.3"),sQuery(id+"F0.wireOp",EDGE,"E8.4"),sQuery(id+"F0.wireOp",EDGE,"E8.5"),subQ5,subQ4,subQ3,subQ2,subQ1,subQ0,sQuery(id+"F1.wireOp",VERTEX,"E11.end")])],"isStart":true}),makeQuery(id+"F3.opExtrude","CAP_FACE",FACE,{"disambiguationData":[OSD([sQuery(id+"F0.wireOp",EDGE,"E1.bottom"),subQ6,sQuery(id+"F0.wireOp",EDGE,"E1.left"),sQuery(id+"F0.wireOp",EDGE,"E1.right"),sQuery(id+"F0.wireOp",EDGE,"E4"),sQuery(id+"F0.wireOp",EDGE,"E5"),sQuery(id+"F0.wireOp",EDGE,"E6"),sQuery(id+"F0.wireOp",EDGE,"E7"),subQ5,subQ4,subQ3,subQ2,subQ1,subQ0])],"isStart":true})]})],"blendedInto":[makeQuery(id+"F3.boolean.opBoolean","MERGE",FACE,{"derivedFrom":[makeQuery(id+"F2.opSweep","CAP_FACE",FACE,{"disambiguationData":[OSD([sQuery(id+"F0.wireOp",EDGE,"E8.0"),sQuery(id+"F0.wireOp",EDGE,"E8.1"),sQuery(id+"F0.wireOp",EDGE,"E8.2"),sQuery(id+"F0.wireOp",EDGE,"E8.3"),sQuery(id+"F0.wireOp",EDGE,"E8.4"),sQuery(id+"F0.wireOp",EDGE,"E8.5"),subQ5,subQ4,subQ3,subQ2,subQ1,subQ0,sQuery(id+"F1.wireOp",VERTEX,"E11.end")])],"isStart":true}),makeQuery(id+"F3.opExtrude","CAP_FACE",FACE,{"disambiguationData":[OSD([sQuery(id+"F0.wireOp",EDGE,"E1.bottom"),subQ6,sQuery(id+"F0.wireOp",EDGE,"E1.left"),sQuery(id+"F0.wireOp",EDGE,"E1.right"),sQuery(id+"F0.wireOp",EDGE,"E4"),sQuery(id+"F0.wireOp",EDGE,"E5"),sQuery(id+"F0.wireOp",EDGE,"E6"),sQuery(id+"F0.wireOp",EDGE,"E7"),subQ5,subQ4,subQ3,subQ2,subQ1,subQ0])],"isStart":true})]})]}),"instanceName":"1"});}
            var Q8;
            {var subQ0=makeQuery(id+"F3.opExtrude","SWEPT_FACE",FACE,{"disambiguationData":[OSD([sQuery(id+"F0.wireOp",EDGE,"E1.left")])]});Q8=makeQuery(id+"F8.opPattern","COPY",EDGE,{"derivedFrom":makeQuery(id+"F5.boolean.opBoolean","INTERSECT",EDGE,{"derivedFrom":[subQ0,makeQuery(id+"F5.opPattern","COPY",FACE,{"derivedFrom":subQ0,"instanceName":"1"})]}),"instanceName":"1"});}
            var Q9;
            {var subQ0=sQuery(id+"F0.wireOp",EDGE,"E9.5");var subQ1=sQuery(id+"F0.wireOp",EDGE,"E9.4");var subQ2=sQuery(id+"F0.wireOp",EDGE,"E9.3");var subQ3=sQuery(id+"F0.wireOp",EDGE,"E9.2");var subQ4=sQuery(id+"F0.wireOp",EDGE,"E9.1");var subQ5=sQuery(id+"F0.wireOp",EDGE,"E9.0");var subQ6=sQuery(id+"F0.wireOp",EDGE,"E1.top");Q9=makeQuery(id+"F8.opPattern","COPY",EDGE,{"derivedFrom":makeQuery(id+"F7.opFillet","BLEND_EDGE",EDGE,{"blendedFrom":[makeQuery(id+"F5.opPattern","COPY",EDGE,{"derivedFrom":makeQuery(id+"F3.opExtrude","CAP_EDGE",EDGE,{"disambiguationData":[OSD([subQ6])],"isStart":false}),"instanceName":"1"}),makeQuery(id+"F5.opPattern","COPY",FACE,{"derivedFrom":makeQuery(id+"F3.boolean.opBoolean","MERGE",FACE,{"derivedFrom":[makeQuery(id+"F2.opSweep","CAP_FACE",FACE,{"disambiguationData":[OSD([sQuery(id+"F0.wireOp",EDGE,"E8.0"),sQuery(id+"F0.wireOp",EDGE,"E8.1"),sQuery(id+"F0.wireOp",EDGE,"E8.2"),sQuery(id+"F0.wireOp",EDGE,"E8.3"),sQuery(id+"F0.wireOp",EDGE,"E8.4"),sQuery(id+"F0.wireOp",EDGE,"E8.5"),subQ5,subQ4,subQ3,subQ2,subQ1,subQ0,sQuery(id+"F1.wireOp",VERTEX,"E11.end")])],"isStart":true}),makeQuery(id+"F3.opExtrude","CAP_FACE",FACE,{"disambiguationData":[OSD([sQuery(id+"F0.wireOp",EDGE,"E1.bottom"),subQ6,sQuery(id+"F0.wireOp",EDGE,"E1.left"),sQuery(id+"F0.wireOp",EDGE,"E1.right"),sQuery(id+"F0.wireOp",EDGE,"E4"),sQuery(id+"F0.wireOp",EDGE,"E5"),sQuery(id+"F0.wireOp",EDGE,"E6"),sQuery(id+"F0.wireOp",EDGE,"E7"),subQ5,subQ4,subQ3,subQ2,subQ1,subQ0])],"isStart":true})]}),"instanceName":"1"})],"blendedInto":[makeQuery(id+"F5.opPattern","COPY",FACE,{"derivedFrom":makeQuery(id+"F3.boolean.opBoolean","MERGE",FACE,{"derivedFrom":[makeQuery(id+"F2.opSweep","CAP_FACE",FACE,{"disambiguationData":[OSD([sQuery(id+"F0.wireOp",EDGE,"E8.0"),sQuery(id+"F0.wireOp",EDGE,"E8.1"),sQuery(id+"F0.wireOp",EDGE,"E8.2"),sQuery(id+"F0.wireOp",EDGE,"E8.3"),sQuery(id+"F0.wireOp",EDGE,"E8.4"),sQuery(id+"F0.wireOp",EDGE,"E8.5"),subQ5,subQ4,subQ3,subQ2,subQ1,subQ0,sQuery(id+"F1.wireOp",VERTEX,"E11.end")])],"isStart":true}),makeQuery(id+"F3.opExtrude","CAP_FACE",FACE,{"disambiguationData":[OSD([sQuery(id+"F0.wireOp",EDGE,"E1.bottom"),subQ6,sQuery(id+"F0.wireOp",EDGE,"E1.left"),sQuery(id+"F0.wireOp",EDGE,"E1.right"),sQuery(id+"F0.wireOp",EDGE,"E4"),sQuery(id+"F0.wireOp",EDGE,"E5"),sQuery(id+"F0.wireOp",EDGE,"E6"),sQuery(id+"F0.wireOp",EDGE,"E7"),subQ5,subQ4,subQ3,subQ2,subQ1,subQ0])],"isStart":true})]}),"instanceName":"1"})]}),"instanceName":"1"});}
            var Q10;
            {var subQ0=sQuery(id+"F0.wireOp",EDGE,"E9.5");var subQ1=sQuery(id+"F0.wireOp",EDGE,"E9.4");var subQ2=sQuery(id+"F0.wireOp",EDGE,"E9.3");var subQ3=sQuery(id+"F0.wireOp",EDGE,"E9.2");var subQ4=sQuery(id+"F0.wireOp",EDGE,"E9.1");var subQ5=sQuery(id+"F0.wireOp",EDGE,"E9.0");var subQ6=sQuery(id+"F0.wireOp",EDGE,"E1.bottom");Q10=makeQuery(id+"F8.opPattern","COPY",EDGE,{"derivedFrom":makeQuery(id+"F7.opFillet","BLEND_EDGE",EDGE,{"blendedFrom":[makeQuery(id+"F5.opPattern","COPY",EDGE,{"derivedFrom":makeQuery(id+"F3.opExtrude","CAP_EDGE",EDGE,{"disambiguationData":[OSD([subQ6])],"isStart":false}),"instanceName":"1"}),makeQuery(id+"F5.opPattern","COPY",FACE,{"derivedFrom":makeQuery(id+"F3.boolean.opBoolean","MERGE",FACE,{"derivedFrom":[makeQuery(id+"F2.opSweep","CAP_FACE",FACE,{"disambiguationData":[OSD([sQuery(id+"F0.wireOp",EDGE,"E8.0"),sQuery(id+"F0.wireOp",EDGE,"E8.1"),sQuery(id+"F0.wireOp",EDGE,"E8.2"),sQuery(id+"F0.wireOp",EDGE,"E8.3"),sQuery(id+"F0.wireOp",EDGE,"E8.4"),sQuery(id+"F0.wireOp",EDGE,"E8.5"),subQ5,subQ4,subQ3,subQ2,subQ1,subQ0,sQuery(id+"F1.wireOp",VERTEX,"E11.end")])],"isStart":true}),makeQuery(id+"F3.opExtrude","CAP_FACE",FACE,{"disambiguationData":[OSD([subQ6,sQuery(id+"F0.wireOp",EDGE,"E1.top"),sQuery(id+"F0.wireOp",EDGE,"E1.left"),sQuery(id+"F0.wireOp",EDGE,"E1.right"),sQuery(id+"F0.wireOp",EDGE,"E4"),sQuery(id+"F0.wireOp",EDGE,"E5"),sQuery(id+"F0.wireOp",EDGE,"E6"),sQuery(id+"F0.wireOp",EDGE,"E7"),subQ5,subQ4,subQ3,subQ2,subQ1,subQ0])],"isStart":true})]}),"instanceName":"1"})],"blendedInto":[makeQuery(id+"F5.opPattern","COPY",FACE,{"derivedFrom":makeQuery(id+"F3.boolean.opBoolean","MERGE",FACE,{"derivedFrom":[makeQuery(id+"F2.opSweep","CAP_FACE",FACE,{"disambiguationData":[OSD([sQuery(id+"F0.wireOp",EDGE,"E8.0"),sQuery(id+"F0.wireOp",EDGE,"E8.1"),sQuery(id+"F0.wireOp",EDGE,"E8.2"),sQuery(id+"F0.wireOp",EDGE,"E8.3"),sQuery(id+"F0.wireOp",EDGE,"E8.4"),sQuery(id+"F0.wireOp",EDGE,"E8.5"),subQ5,subQ4,subQ3,subQ2,subQ1,subQ0,sQuery(id+"F1.wireOp",VERTEX,"E11.end")])],"isStart":true}),makeQuery(id+"F3.opExtrude","CAP_FACE",FACE,{"disambiguationData":[OSD([subQ6,sQuery(id+"F0.wireOp",EDGE,"E1.top"),sQuery(id+"F0.wireOp",EDGE,"E1.left"),sQuery(id+"F0.wireOp",EDGE,"E1.right"),sQuery(id+"F0.wireOp",EDGE,"E4"),sQuery(id+"F0.wireOp",EDGE,"E5"),sQuery(id+"F0.wireOp",EDGE,"E6"),sQuery(id+"F0.wireOp",EDGE,"E7"),subQ5,subQ4,subQ3,subQ2,subQ1,subQ0])],"isStart":true})]}),"instanceName":"1"})]}),"instanceName":"1"});}
            var Q11;
            {var subQ0=sQuery(id+"F0.wireOp",EDGE,"E9.5");var subQ1=sQuery(id+"F0.wireOp",EDGE,"E9.4");var subQ2=sQuery(id+"F0.wireOp",EDGE,"E9.3");var subQ3=sQuery(id+"F0.wireOp",EDGE,"E9.2");var subQ4=sQuery(id+"F0.wireOp",EDGE,"E9.1");var subQ5=sQuery(id+"F0.wireOp",EDGE,"E9.0");var subQ6=sQuery(id+"F0.wireOp",EDGE,"E1.right");Q11=makeQuery(id+"F8.opPattern","COPY",EDGE,{"derivedFrom":makeQuery(id+"F7.opFillet","BLEND_EDGE",EDGE,{"blendedFrom":[makeQuery(id+"F5.opPattern","COPY",EDGE,{"derivedFrom":makeQuery(id+"F3.opExtrude","CAP_EDGE",EDGE,{"disambiguationData":[OSD([subQ6])],"isStart":false}),"instanceName":"1"}),makeQuery(id+"F5.opPattern","COPY",FACE,{"derivedFrom":makeQuery(id+"F3.boolean.opBoolean","MERGE",FACE,{"derivedFrom":[makeQuery(id+"F2.opSweep","CAP_FACE",FACE,{"disambiguationData":[OSD([sQuery(id+"F0.wireOp",EDGE,"E8.0"),sQuery(id+"F0.wireOp",EDGE,"E8.1"),sQuery(id+"F0.wireOp",EDGE,"E8.2"),sQuery(id+"F0.wireOp",EDGE,"E8.3"),sQuery(id+"F0.wireOp",EDGE,"E8.4"),sQuery(id+"F0.wireOp",EDGE,"E8.5"),subQ5,subQ4,subQ3,subQ2,subQ1,subQ0,sQuery(id+"F1.wireOp",VERTEX,"E11.end")])],"isStart":true}),makeQuery(id+"F3.opExtrude","CAP_FACE",FACE,{"disambiguationData":[OSD([sQuery(id+"F0.wireOp",EDGE,"E1.bottom"),sQuery(id+"F0.wireOp",EDGE,"E1.top"),sQuery(id+"F0.wireOp",EDGE,"E1.left"),subQ6,sQuery(id+"F0.wireOp",EDGE,"E4"),sQuery(id+"F0.wireOp",EDGE,"E5"),sQuery(id+"F0.wireOp",EDGE,"E6"),sQuery(id+"F0.wireOp",EDGE,"E7"),subQ5,subQ4,subQ3,subQ2,subQ1,subQ0])],"isStart":true})]}),"instanceName":"1"})],"blendedInto":[makeQuery(id+"F5.opPattern","COPY",FACE,{"derivedFrom":makeQuery(id+"F3.boolean.opBoolean","MERGE",FACE,{"derivedFrom":[makeQuery(id+"F2.opSweep","CAP_FACE",FACE,{"disambiguationData":[OSD([sQuery(id+"F0.wireOp",EDGE,"E8.0"),sQuery(id+"F0.wireOp",EDGE,"E8.1"),sQuery(id+"F0.wireOp",EDGE,"E8.2"),sQuery(id+"F0.wireOp",EDGE,"E8.3"),sQuery(id+"F0.wireOp",EDGE,"E8.4"),sQuery(id+"F0.wireOp",EDGE,"E8.5"),subQ5,subQ4,subQ3,subQ2,subQ1,subQ0,sQuery(id+"F1.wireOp",VERTEX,"E11.end")])],"isStart":true}),makeQuery(id+"F3.opExtrude","CAP_FACE",FACE,{"disambiguationData":[OSD([sQuery(id+"F0.wireOp",EDGE,"E1.bottom"),sQuery(id+"F0.wireOp",EDGE,"E1.top"),sQuery(id+"F0.wireOp",EDGE,"E1.left"),subQ6,sQuery(id+"F0.wireOp",EDGE,"E4"),sQuery(id+"F0.wireOp",EDGE,"E5"),sQuery(id+"F0.wireOp",EDGE,"E6"),sQuery(id+"F0.wireOp",EDGE,"E7"),subQ5,subQ4,subQ3,subQ2,subQ1,subQ0])],"isStart":true})]}),"instanceName":"1"})]}),"instanceName":"1"});}
            var Q12;
            {var subQ0=sQuery(id+"F0.wireOp",EDGE,"E9.5");var subQ1=sQuery(id+"F0.wireOp",EDGE,"E9.4");var subQ2=sQuery(id+"F0.wireOp",EDGE,"E9.3");var subQ3=sQuery(id+"F0.wireOp",EDGE,"E9.2");var subQ4=sQuery(id+"F0.wireOp",EDGE,"E9.1");var subQ5=sQuery(id+"F0.wireOp",EDGE,"E9.0");var subQ6=sQuery(id+"F0.wireOp",EDGE,"E1.right");Q12=makeQuery(id+"F7.opFillet","BLEND_EDGE",EDGE,{"blendedFrom":[makeQuery(id+"F5.opPattern","COPY",EDGE,{"derivedFrom":makeQuery(id+"F3.opExtrude","CAP_EDGE",EDGE,{"disambiguationData":[OSD([subQ6])],"isStart":false}),"instanceName":"1"}),makeQuery(id+"F5.opPattern","COPY",FACE,{"derivedFrom":makeQuery(id+"F3.boolean.opBoolean","MERGE",FACE,{"derivedFrom":[makeQuery(id+"F2.opSweep","CAP_FACE",FACE,{"disambiguationData":[OSD([sQuery(id+"F0.wireOp",EDGE,"E8.0"),sQuery(id+"F0.wireOp",EDGE,"E8.1"),sQuery(id+"F0.wireOp",EDGE,"E8.2"),sQuery(id+"F0.wireOp",EDGE,"E8.3"),sQuery(id+"F0.wireOp",EDGE,"E8.4"),sQuery(id+"F0.wireOp",EDGE,"E8.5"),subQ5,subQ4,subQ3,subQ2,subQ1,subQ0,sQuery(id+"F1.wireOp",VERTEX,"E11.end")])],"isStart":true}),makeQuery(id+"F3.opExtrude","CAP_FACE",FACE,{"disambiguationData":[OSD([sQuery(id+"F0.wireOp",EDGE,"E1.bottom"),sQuery(id+"F0.wireOp",EDGE,"E1.top"),sQuery(id+"F0.wireOp",EDGE,"E1.left"),subQ6,sQuery(id+"F0.wireOp",EDGE,"E4"),sQuery(id+"F0.wireOp",EDGE,"E5"),sQuery(id+"F0.wireOp",EDGE,"E6"),sQuery(id+"F0.wireOp",EDGE,"E7"),subQ5,subQ4,subQ3,subQ2,subQ1,subQ0])],"isStart":true})]}),"instanceName":"1"})],"blendedInto":[makeQuery(id+"F5.opPattern","COPY",FACE,{"derivedFrom":makeQuery(id+"F3.boolean.opBoolean","MERGE",FACE,{"derivedFrom":[makeQuery(id+"F2.opSweep","CAP_FACE",FACE,{"disambiguationData":[OSD([sQuery(id+"F0.wireOp",EDGE,"E8.0"),sQuery(id+"F0.wireOp",EDGE,"E8.1"),sQuery(id+"F0.wireOp",EDGE,"E8.2"),sQuery(id+"F0.wireOp",EDGE,"E8.3"),sQuery(id+"F0.wireOp",EDGE,"E8.4"),sQuery(id+"F0.wireOp",EDGE,"E8.5"),subQ5,subQ4,subQ3,subQ2,subQ1,subQ0,sQuery(id+"F1.wireOp",VERTEX,"E11.end")])],"isStart":true}),makeQuery(id+"F3.opExtrude","CAP_FACE",FACE,{"disambiguationData":[OSD([sQuery(id+"F0.wireOp",EDGE,"E1.bottom"),sQuery(id+"F0.wireOp",EDGE,"E1.top"),sQuery(id+"F0.wireOp",EDGE,"E1.left"),subQ6,sQuery(id+"F0.wireOp",EDGE,"E4"),sQuery(id+"F0.wireOp",EDGE,"E5"),sQuery(id+"F0.wireOp",EDGE,"E6"),sQuery(id+"F0.wireOp",EDGE,"E7"),subQ5,subQ4,subQ3,subQ2,subQ1,subQ0])],"isStart":true})]}),"instanceName":"1"})]});}
            var Q13;
            {var subQ0=sQuery(id+"F0.wireOp",EDGE,"E9.5");var subQ1=sQuery(id+"F0.wireOp",EDGE,"E9.4");var subQ2=sQuery(id+"F0.wireOp",EDGE,"E9.3");var subQ3=sQuery(id+"F0.wireOp",EDGE,"E9.2");var subQ4=sQuery(id+"F0.wireOp",EDGE,"E9.1");var subQ5=sQuery(id+"F0.wireOp",EDGE,"E9.0");var subQ6=sQuery(id+"F0.wireOp",EDGE,"E1.top");Q13=makeQuery(id+"F7.opFillet","BLEND_EDGE",EDGE,{"blendedFrom":[makeQuery(id+"F5.opPattern","COPY",EDGE,{"derivedFrom":makeQuery(id+"F3.opExtrude","CAP_EDGE",EDGE,{"disambiguationData":[OSD([subQ6])],"isStart":false}),"instanceName":"1"}),makeQuery(id+"F5.opPattern","COPY",FACE,{"derivedFrom":makeQuery(id+"F3.boolean.opBoolean","MERGE",FACE,{"derivedFrom":[makeQuery(id+"F2.opSweep","CAP_FACE",FACE,{"disambiguationData":[OSD([sQuery(id+"F0.wireOp",EDGE,"E8.0"),sQuery(id+"F0.wireOp",EDGE,"E8.1"),sQuery(id+"F0.wireOp",EDGE,"E8.2"),sQuery(id+"F0.wireOp",EDGE,"E8.3"),sQuery(id+"F0.wireOp",EDGE,"E8.4"),sQuery(id+"F0.wireOp",EDGE,"E8.5"),subQ5,subQ4,subQ3,subQ2,subQ1,subQ0,sQuery(id+"F1.wireOp",VERTEX,"E11.end")])],"isStart":true}),makeQuery(id+"F3.opExtrude","CAP_FACE",FACE,{"disambiguationData":[OSD([sQuery(id+"F0.wireOp",EDGE,"E1.bottom"),subQ6,sQuery(id+"F0.wireOp",EDGE,"E1.left"),sQuery(id+"F0.wireOp",EDGE,"E1.right"),sQuery(id+"F0.wireOp",EDGE,"E4"),sQuery(id+"F0.wireOp",EDGE,"E5"),sQuery(id+"F0.wireOp",EDGE,"E6"),sQuery(id+"F0.wireOp",EDGE,"E7"),subQ5,subQ4,subQ3,subQ2,subQ1,subQ0])],"isStart":true})]}),"instanceName":"1"})],"blendedInto":[makeQuery(id+"F5.opPattern","COPY",FACE,{"derivedFrom":makeQuery(id+"F3.boolean.opBoolean","MERGE",FACE,{"derivedFrom":[makeQuery(id+"F2.opSweep","CAP_FACE",FACE,{"disambiguationData":[OSD([sQuery(id+"F0.wireOp",EDGE,"E8.0"),sQuery(id+"F0.wireOp",EDGE,"E8.1"),sQuery(id+"F0.wireOp",EDGE,"E8.2"),sQuery(id+"F0.wireOp",EDGE,"E8.3"),sQuery(id+"F0.wireOp",EDGE,"E8.4"),sQuery(id+"F0.wireOp",EDGE,"E8.5"),subQ5,subQ4,subQ3,subQ2,subQ1,subQ0,sQuery(id+"F1.wireOp",VERTEX,"E11.end")])],"isStart":true}),makeQuery(id+"F3.opExtrude","CAP_FACE",FACE,{"disambiguationData":[OSD([sQuery(id+"F0.wireOp",EDGE,"E1.bottom"),subQ6,sQuery(id+"F0.wireOp",EDGE,"E1.left"),sQuery(id+"F0.wireOp",EDGE,"E1.right"),sQuery(id+"F0.wireOp",EDGE,"E4"),sQuery(id+"F0.wireOp",EDGE,"E5"),sQuery(id+"F0.wireOp",EDGE,"E6"),sQuery(id+"F0.wireOp",EDGE,"E7"),subQ5,subQ4,subQ3,subQ2,subQ1,subQ0])],"isStart":true})]}),"instanceName":"1"})]});}
            var Q14;
            {var subQ0=sQuery(id+"F0.wireOp",EDGE,"E9.5");var subQ1=sQuery(id+"F0.wireOp",EDGE,"E9.4");var subQ2=sQuery(id+"F0.wireOp",EDGE,"E9.3");var subQ3=sQuery(id+"F0.wireOp",EDGE,"E9.2");var subQ4=sQuery(id+"F0.wireOp",EDGE,"E9.1");var subQ5=sQuery(id+"F0.wireOp",EDGE,"E9.0");var subQ6=sQuery(id+"F0.wireOp",EDGE,"E1.bottom");Q14=makeQuery(id+"F7.opFillet","BLEND_EDGE",EDGE,{"blendedFrom":[makeQuery(id+"F5.opPattern","COPY",EDGE,{"derivedFrom":makeQuery(id+"F3.opExtrude","CAP_EDGE",EDGE,{"disambiguationData":[OSD([subQ6])],"isStart":false}),"instanceName":"1"}),makeQuery(id+"F5.opPattern","COPY",FACE,{"derivedFrom":makeQuery(id+"F3.boolean.opBoolean","MERGE",FACE,{"derivedFrom":[makeQuery(id+"F2.opSweep","CAP_FACE",FACE,{"disambiguationData":[OSD([sQuery(id+"F0.wireOp",EDGE,"E8.0"),sQuery(id+"F0.wireOp",EDGE,"E8.1"),sQuery(id+"F0.wireOp",EDGE,"E8.2"),sQuery(id+"F0.wireOp",EDGE,"E8.3"),sQuery(id+"F0.wireOp",EDGE,"E8.4"),sQuery(id+"F0.wireOp",EDGE,"E8.5"),subQ5,subQ4,subQ3,subQ2,subQ1,subQ0,sQuery(id+"F1.wireOp",VERTEX,"E11.end")])],"isStart":true}),makeQuery(id+"F3.opExtrude","CAP_FACE",FACE,{"disambiguationData":[OSD([subQ6,sQuery(id+"F0.wireOp",EDGE,"E1.top"),sQuery(id+"F0.wireOp",EDGE,"E1.left"),sQuery(id+"F0.wireOp",EDGE,"E1.right"),sQuery(id+"F0.wireOp",EDGE,"E4"),sQuery(id+"F0.wireOp",EDGE,"E5"),sQuery(id+"F0.wireOp",EDGE,"E6"),sQuery(id+"F0.wireOp",EDGE,"E7"),subQ5,subQ4,subQ3,subQ2,subQ1,subQ0])],"isStart":true})]}),"instanceName":"1"})],"blendedInto":[makeQuery(id+"F5.opPattern","COPY",FACE,{"derivedFrom":makeQuery(id+"F3.boolean.opBoolean","MERGE",FACE,{"derivedFrom":[makeQuery(id+"F2.opSweep","CAP_FACE",FACE,{"disambiguationData":[OSD([sQuery(id+"F0.wireOp",EDGE,"E8.0"),sQuery(id+"F0.wireOp",EDGE,"E8.1"),sQuery(id+"F0.wireOp",EDGE,"E8.2"),sQuery(id+"F0.wireOp",EDGE,"E8.3"),sQuery(id+"F0.wireOp",EDGE,"E8.4"),sQuery(id+"F0.wireOp",EDGE,"E8.5"),subQ5,subQ4,subQ3,subQ2,subQ1,subQ0,sQuery(id+"F1.wireOp",VERTEX,"E11.end")])],"isStart":true}),makeQuery(id+"F3.opExtrude","CAP_FACE",FACE,{"disambiguationData":[OSD([subQ6,sQuery(id+"F0.wireOp",EDGE,"E1.top"),sQuery(id+"F0.wireOp",EDGE,"E1.left"),sQuery(id+"F0.wireOp",EDGE,"E1.right"),sQuery(id+"F0.wireOp",EDGE,"E4"),sQuery(id+"F0.wireOp",EDGE,"E5"),sQuery(id+"F0.wireOp",EDGE,"E6"),sQuery(id+"F0.wireOp",EDGE,"E7"),subQ5,subQ4,subQ3,subQ2,subQ1,subQ0])],"isStart":true})]}),"instanceName":"1"})]});}
            chamfer(context, id + "F12", {"entities" : qUnion([Q0, Q1, Q2, Q3, Q4, Q5, Q6, Q7, Q8, Q9, Q10, Q11, Q12, Q13, Q14]), "width" : 1.33 * mm, "tangentPropagation" : true});
        }
        {
            var Q0;
            {var subQ0=sQuery(id+"F0.wireOp",EDGE,"E1.left");var subQ2=sQuery(id+"F0.wireOp",EDGE,"E1.bottom");var subQ3=makeQuery(id+"F3.opExtrude","SWEPT_FACE",FACE,{"disambiguationData":[OSD([subQ2])]});Q0=makeQuery(id+"F11.boolean.opBoolean","SPLIT",EDGE,{"disambiguationData":[TD([subQ3])],"derivedFrom":makeQuery(id+"F3.opExtrude","CAP_EDGE",EDGE,{"disambiguationData":[OSD([subQ0])],"isStart":true})});}
            var Q1;
            {var subQ0=sQuery(id+"F0.wireOp",EDGE,"E1.left");var subQ1=sQuery(id+"F0.wireOp",EDGE,"E1.top");var subQ2=makeQuery(id+"F3.opExtrude","SWEPT_FACE",FACE,{"disambiguationData":[OSD([subQ1])]});Q1=makeQuery(id+"F11.boolean.opBoolean","SPLIT",EDGE,{"disambiguationData":[TD([subQ2])],"derivedFrom":makeQuery(id+"F3.opExtrude","CAP_EDGE",EDGE,{"disambiguationData":[OSD([subQ0])],"isStart":true})});}
            chamfer(context, id + "F13", {"entities" : qUnion([Q0, Q1]), "width" : 1.31 * mm, "tangentPropagation" : true});
        }
        {
            var Q0;
            Q0=makeQuery(id+"F8.opPattern","COPY",EDGE,{"derivedFrom":makeQuery(id+"F5.opPattern","COPY",EDGE,{"derivedFrom":makeQuery(id+"F2.opSweep","CAP_EDGE",EDGE,{"disambiguationData":[OSD([sQuery(id+"F0.wireOp",EDGE,"E9.5"),sQuery(id+"F1.wireOp",VERTEX,"E11.end")])],"isStart":true}),"instanceName":"1"}),"instanceName":"1"});
            var Q1;
            Q1=makeQuery(id+"F8.opPattern","COPY",EDGE,{"derivedFrom":makeQuery(id+"F5.opPattern","COPY",EDGE,{"derivedFrom":makeQuery(id+"F2.opSweep","CAP_EDGE",EDGE,{"disambiguationData":[OSD([sQuery(id+"F0.wireOp",EDGE,"E9.0"),sQuery(id+"F1.wireOp",VERTEX,"E11.end")])],"isStart":true}),"instanceName":"1"}),"instanceName":"1"});
            var Q2;
            Q2=makeQuery(id+"F8.opPattern","COPY",EDGE,{"derivedFrom":makeQuery(id+"F5.opPattern","COPY",EDGE,{"derivedFrom":makeQuery(id+"F2.opSweep","CAP_EDGE",EDGE,{"disambiguationData":[OSD([sQuery(id+"F0.wireOp",EDGE,"E9.3"),sQuery(id+"F1.wireOp",VERTEX,"E11.end")])],"isStart":true}),"instanceName":"1"}),"instanceName":"1"});
            var Q3;
            {var subQ0=sQuery(id+"F0.wireOp",EDGE,"E9.2");Q3=makeQuery(id+"F8.opPattern","COPY",EDGE,{"derivedFrom":makeQuery(id+"F5.opPattern","COPY",EDGE,{"derivedFrom":makeQuery(id+"F3.boolean.opBoolean","MERGE",EDGE,{"derivedFrom":[makeQuery(id+"F2.opSweep","CAP_EDGE",EDGE,{"disambiguationData":[OSD([subQ0,sQuery(id+"F1.wireOp",VERTEX,"E11.end")])],"isStart":true}),makeQuery(id+"F3.opExtrude","CAP_EDGE",EDGE,{"disambiguationData":[OSD([subQ0])],"isStart":true})]}),"instanceName":"1"}),"instanceName":"1"});}
            var Q4;
            {var subQ0=sQuery(id+"F0.wireOp",EDGE,"E9.1");Q4=makeQuery(id+"F8.opPattern","COPY",EDGE,{"derivedFrom":makeQuery(id+"F5.opPattern","COPY",EDGE,{"derivedFrom":makeQuery(id+"F3.boolean.opBoolean","MERGE",EDGE,{"derivedFrom":[makeQuery(id+"F2.opSweep","CAP_EDGE",EDGE,{"disambiguationData":[OSD([subQ0,sQuery(id+"F1.wireOp",VERTEX,"E11.end")])],"isStart":true}),makeQuery(id+"F3.opExtrude","CAP_EDGE",EDGE,{"disambiguationData":[OSD([subQ0])],"isStart":true})]}),"instanceName":"1"}),"instanceName":"1"});}
            var Q5;
            {var subQ0=sQuery(id+"F0.wireOp",EDGE,"E9.4");Q5=makeQuery(id+"F8.opPattern","COPY",EDGE,{"derivedFrom":makeQuery(id+"F5.opPattern","COPY",EDGE,{"derivedFrom":makeQuery(id+"F3.boolean.opBoolean","MERGE",EDGE,{"derivedFrom":[makeQuery(id+"F2.opSweep","CAP_EDGE",EDGE,{"disambiguationData":[OSD([subQ0,sQuery(id+"F1.wireOp",VERTEX,"E11.end")])],"isStart":true}),makeQuery(id+"F3.opExtrude","CAP_EDGE",EDGE,{"disambiguationData":[OSD([subQ0])],"isStart":true})]}),"instanceName":"1"}),"instanceName":"1"});}
            var Q6;
            {var subQ0=sQuery(id+"F0.wireOp",EDGE,"E9.1");Q6=makeQuery(id+"F5.opPattern","COPY",EDGE,{"derivedFrom":makeQuery(id+"F3.boolean.opBoolean","MERGE",EDGE,{"derivedFrom":[makeQuery(id+"F2.opSweep","CAP_EDGE",EDGE,{"disambiguationData":[OSD([subQ0,sQuery(id+"F1.wireOp",VERTEX,"E11.end")])],"isStart":true}),makeQuery(id+"F3.opExtrude","CAP_EDGE",EDGE,{"disambiguationData":[OSD([subQ0])],"isStart":true})]}),"instanceName":"1"});}
            var Q7;
            Q7=makeQuery(id+"F5.opPattern","COPY",EDGE,{"derivedFrom":makeQuery(id+"F2.opSweep","CAP_EDGE",EDGE,{"disambiguationData":[OSD([sQuery(id+"F0.wireOp",EDGE,"E9.3"),sQuery(id+"F1.wireOp",VERTEX,"E11.end")])],"isStart":true}),"instanceName":"1"});
            var Q8;
            Q8=makeQuery(id+"F5.opPattern","COPY",EDGE,{"derivedFrom":makeQuery(id+"F2.opSweep","CAP_EDGE",EDGE,{"disambiguationData":[OSD([sQuery(id+"F0.wireOp",EDGE,"E9.0"),sQuery(id+"F1.wireOp",VERTEX,"E11.end")])],"isStart":true}),"instanceName":"1"});
            var Q9;
            Q9=makeQuery(id+"F5.opPattern","COPY",EDGE,{"derivedFrom":makeQuery(id+"F2.opSweep","CAP_EDGE",EDGE,{"disambiguationData":[OSD([sQuery(id+"F0.wireOp",EDGE,"E9.5"),sQuery(id+"F1.wireOp",VERTEX,"E11.end")])],"isStart":true}),"instanceName":"1"});
            var Q10;
            {var subQ0=sQuery(id+"F0.wireOp",EDGE,"E9.4");Q10=makeQuery(id+"F5.opPattern","COPY",EDGE,{"derivedFrom":makeQuery(id+"F3.boolean.opBoolean","MERGE",EDGE,{"derivedFrom":[makeQuery(id+"F2.opSweep","CAP_EDGE",EDGE,{"disambiguationData":[OSD([subQ0,sQuery(id+"F1.wireOp",VERTEX,"E11.end")])],"isStart":true}),makeQuery(id+"F3.opExtrude","CAP_EDGE",EDGE,{"disambiguationData":[OSD([subQ0])],"isStart":true})]}),"instanceName":"1"});}
            var Q11;
            {var subQ0=sQuery(id+"F0.wireOp",EDGE,"E9.2");Q11=makeQuery(id+"F5.opPattern","COPY",EDGE,{"derivedFrom":makeQuery(id+"F3.boolean.opBoolean","MERGE",EDGE,{"derivedFrom":[makeQuery(id+"F2.opSweep","CAP_EDGE",EDGE,{"disambiguationData":[OSD([subQ0,sQuery(id+"F1.wireOp",VERTEX,"E11.end")])],"isStart":true}),makeQuery(id+"F3.opExtrude","CAP_EDGE",EDGE,{"disambiguationData":[OSD([subQ0])],"isStart":true})]}),"instanceName":"1"});}
            chamfer(context, id + "F14", {"entities" : qUnion([Q0, Q1, Q2, Q3, Q4, Q5, Q6, Q7, Q8, Q9, Q10, Q11]), "width" : 3 * mm});
        }
    });
